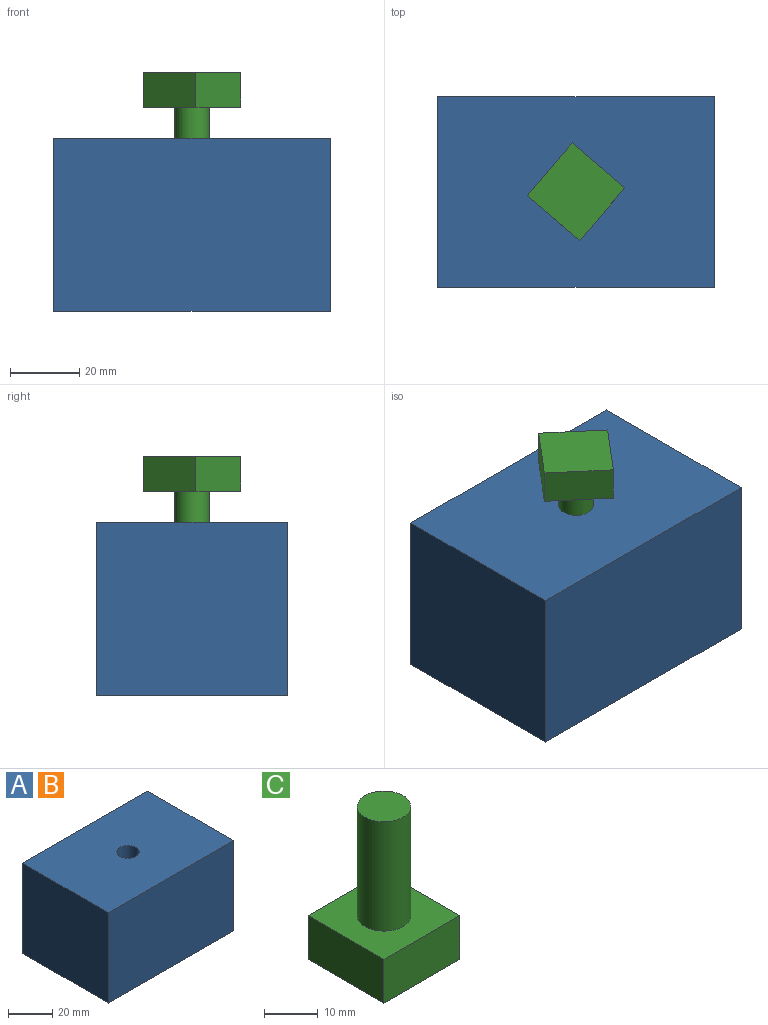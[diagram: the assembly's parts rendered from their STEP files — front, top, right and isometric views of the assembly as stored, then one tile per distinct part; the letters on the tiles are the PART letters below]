
ASSEMBLY  parts=3 mates=1
PART A: 8 faces, bbox 80x55x50 mm
  f0: plane 55x50mm, normal (1,0,0), area 2750mm2, adj f1,f3,f4,f5
  f1: plane 80x50mm, normal (0,1,0), area 4000mm2, adj f0,f2,f4,f5
  f2: plane 55x50mm, normal (-1,0,0), area 2750mm2, adj f1,f3,f4,f5
  f3: plane 80x50mm, normal (0,-1,0), area 4000mm2, adj f0,f2,f4,f5
  f4: plane 80x55mm, normal (0,0,1), area 4321.5mm2, adj f0,f1,f2,f3,f6
  f5: plane 80x55mm, normal (0,0,-1), area 4400mm2, adj f0,f1,f2,f3
  f6: cylinder r=5mm len=25mm, axis (0,0,1), area 785.4mm2, adj f4,f7
  f7: plane 10x10mm, normal (0,0,1), area 78.5mm2, adj f6
PART B: same geometry as A
PART C: 8 faces, bbox 20x20x35 mm
  f0: plane 20x10mm, normal (1,0,0), area 200mm2, adj f1,f3,f4,f5
  f1: plane 20x10mm, normal (0,1,0), area 200mm2, adj f0,f2,f4,f5
  f2: plane 20x10mm, normal (-1,0,0), area 200mm2, adj f1,f3,f4,f5
  f3: plane 20x10mm, normal (0,-1,0), area 200mm2, adj f0,f2,f4,f5
  f4: plane 20x20mm, normal (0,0,1), area 321.5mm2, adj f0,f1,f2,f3,f6
  f5: plane 20x20mm, normal (0,0,-1), area 400mm2, adj f0,f1,f2,f3
  f6: cylinder r=5mm len=25mm, axis (0,0,-1), area 785.4mm2, adj f4,f7
  f7: plane 10x10mm, normal (0,0,1), area 78.5mm2, adj f6
PLACE A at identity fixed
PLACE B at identity
PLACE C rot(axis=(-0.91,-0.42,0),180deg) t=(0,0,69.05)mm
MATE cylindrical C.f6 <-> A.f6  axis (0,0,1) through (0,0,46.55)mm
